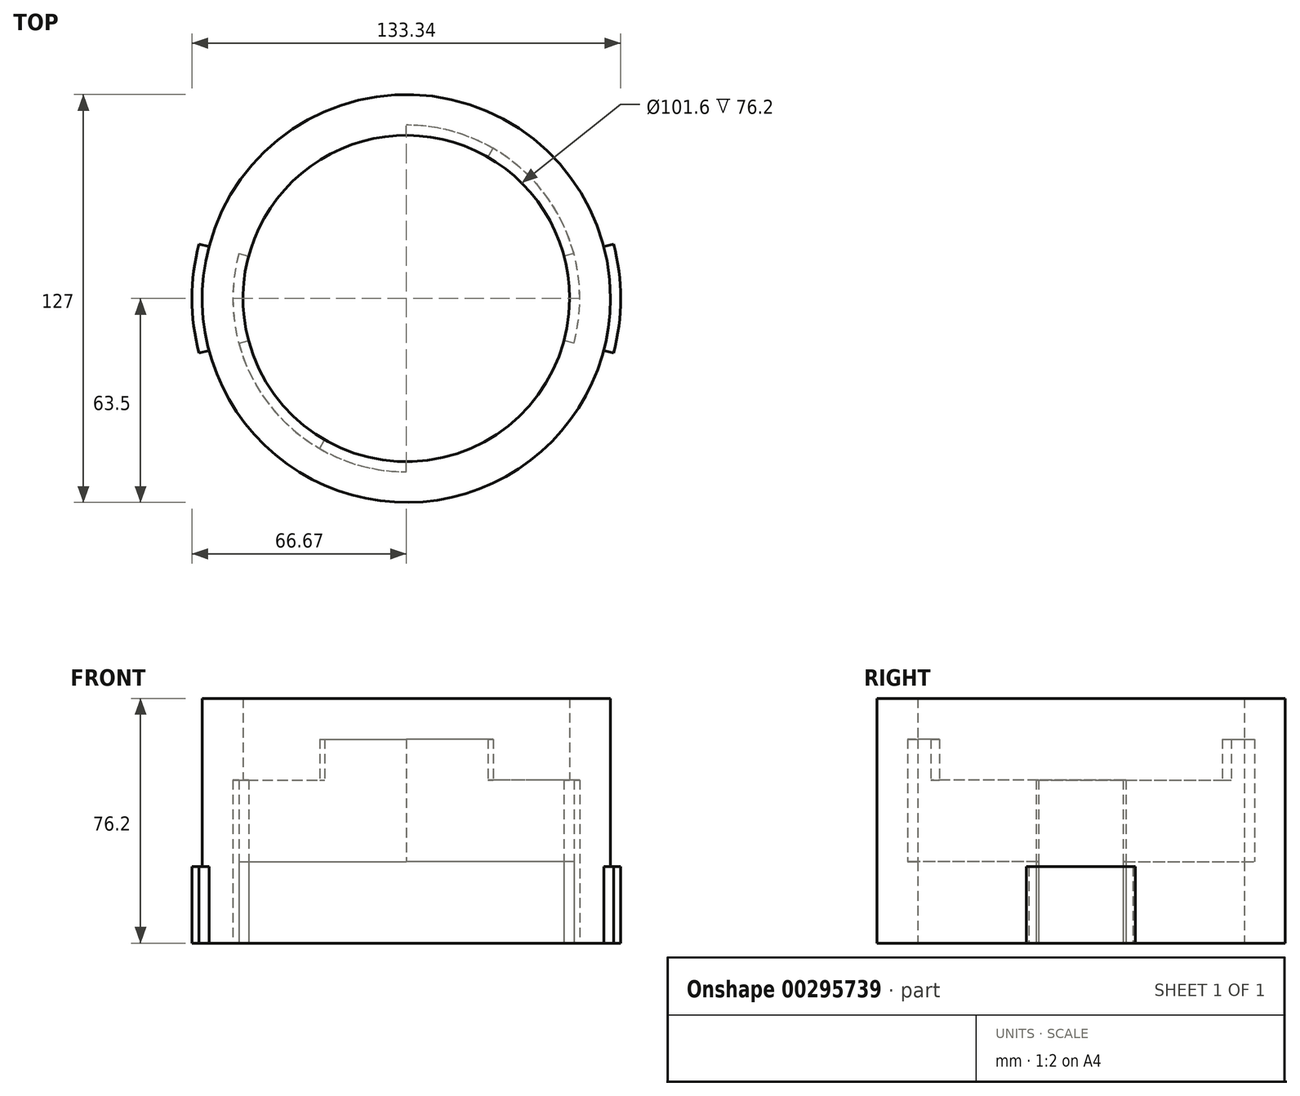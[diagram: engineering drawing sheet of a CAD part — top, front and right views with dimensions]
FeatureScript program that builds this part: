
annotation { "Feature Type Name" : "Feature", "Feature Type Description" : "" }
export const myFeature = defineFeature(function(context is Context, id is Id, definition is map)
    precondition{}
    {
        {
            var Q0;
            Q0=qCreatedBy(makeId("Top.planeOp"),FACE);
            var sketch = newSketch(context, id + "F0", { "sketchPlane" : qUnion([Q0])});
            skCircle(sketch, "E0", {"center": v(0, 0) * mm, "radius": 63.5 * mm});
            skCircle(sketch, "E1", {"center": v(0, 0) * mm, "radius": 50.8 * mm});
            skCircle(sketch, "E2", {"center": v(0, 0) * mm, "radius": 53.98 * mm});
            skArc(sketch, "E3", {"start": v(-64.48, 16.98) * mm, "mid": v(-66.68, 0) * mm, "end": v(-64.48, -16.98) * mm});
            skLineSegment(sketch, "E4.trimOffspring", {"start": v(-61.4, -16.17) * mm, "end": v(-64.48, -16.98) * mm});
            skArc(sketch, "E5.trimOffspring", {"start": v(64.48, -16.98) * mm, "mid": v(66.68, 0) * mm, "end": v(64.48, 16.98) * mm});
            skLineSegment(sketch, "E6.MirrorCS", {"start": v(-61.4, 16.17) * mm, "end": v(-64.48, 16.98) * mm});
            skLineSegment(sketch, "E7.MirrorCS", {"start": v(61.4, -16.17) * mm, "end": v(64.48, -16.98) * mm});
            skLineSegment(sketch, "E8.MirrorCS", {"start": v(61.4, 16.17) * mm, "end": v(64.48, 16.98) * mm});
            skLineSegment(sketch, "E9", {"start": v(0, -53.98) * mm, "end": v(0, -50.8) * mm});
            skLineSegment(sketch, "E10.trimOffspring", {"start": v(0, 50.8) * mm, "end": v(0, 53.98) * mm});
            skLineSegment(sketch, "E11", {"start": v(-26.99, -46.74) * mm, "end": v(-25.4, -44) * mm});
            skLineSegment(sketch, "E12.trimOffspring", {"start": v(25.4, 44) * mm, "end": v(26.99, 46.74) * mm});
            skLineSegment(sketch, "E13", {"start": v(-52.14, -13.97) * mm, "end": v(-49.07, -13.15) * mm});
            skLineSegment(sketch, "E14.MirrorCS", {"start": v(-52.14, 13.97) * mm, "end": v(-49.07, 13.15) * mm});
            skLineSegment(sketch, "E15.MirrorCS", {"start": v(52.14, -13.97) * mm, "end": v(49.07, -13.15) * mm});
            skLineSegment(sketch, "E16.MirrorCS", {"start": v(52.14, 13.97) * mm, "end": v(49.07, 13.15) * mm});
            skSolve(sketch);
        }
        {
            var Q0;
            {var subQ0=sQuery(id+"F0.wireOp",EDGE,"E0");var subQ4=makeQuery(id+"F0.imprint","INTERSECT",VERTEX,{"derivedFrom":[subQ0,sQuery(id+"F0.wireOp",EDGE,"6ba6cb8d-4ce4-45d0-8e24-ed4901a20c0e.trimOffspring")]});Q0=makeQuery(id+"F0.imprint","IMPRINT",FACE,{"disambiguationData":[TD([[makeQuery(id+"F0.imprint","IMPRINT",EDGE,{"disambiguationData":[TD([[subQ4,1.0]])],"derivedFrom":subQ0}),1.0]])]});}
            var Q1;
            {var subQ0=sQuery(id+"F0.wireOp",EDGE,"qwwPtYaD-yE2g-ikrO-oplh-1dd26EcHEVAW");Q1=makeQuery(id+"F0.imprint","IMPRINT",FACE,{"disambiguationData":[TD([[makeQuery(id+"F0.imprint","IMPRINT",EDGE,{"derivedFrom":subQ0}),1.0]])]});}
            var Q2;
            {var subQ0=sQuery(id+"F0.wireOp",EDGE,"qwwPtYaD-yE2g-ikrO-oplh-1dd26EcHEVAW");Q2=makeQuery(id+"F0.imprint","IMPRINT",FACE,{"disambiguationData":[TD([[makeQuery(id+"F0.imprint","IMPRINT",EDGE,{"derivedFrom":subQ0}),-1.0]])]});}
            var Q3;
            {var subQ0=sQuery(id+"F0.wireOp",EDGE,"409aa395-0444-4f70-a1e5-7bc4308f40760.MirrorCS");Q3=makeQuery(id+"F0.imprint","IMPRINT",FACE,{"disambiguationData":[TD([[makeQuery(id+"F0.imprint","IMPRINT",EDGE,{"derivedFrom":subQ0}),-1.0]])]});}
            var Q4;
            {var subQ0=sQuery(id+"F0.wireOp",EDGE,"fd11b51b-482c-4218-80d9-868a347ca85e0.MirrorCS");Q4=makeQuery(id+"F0.imprint","IMPRINT",FACE,{"disambiguationData":[TD([[makeQuery(id+"F0.imprint","IMPRINT",EDGE,{"derivedFrom":subQ0}),1.0]])]});}
            var Q5;
            {var subQ0=sQuery(id+"F0.wireOp",EDGE,"E11");Q5=makeQuery(id+"F0.imprint","IMPRINT",FACE,{"disambiguationData":[TD([[makeQuery(id+"F0.imprint","IMPRINT",EDGE,{"derivedFrom":subQ0}),1.0]])]});}
            var Q6;
            {var subQ0=sQuery(id+"F0.wireOp",EDGE,"E13");Q6=makeQuery(id+"F0.imprint","IMPRINT",FACE,{"disambiguationData":[TD([[makeQuery(id+"F0.imprint","IMPRINT",EDGE,{"derivedFrom":subQ0}),1.0]])]});}
            var Q7;
            {var subQ0=sQuery(id+"F0.wireOp",EDGE,"E10.trimOffspring");Q7=makeQuery(id+"F0.imprint","IMPRINT",FACE,{"disambiguationData":[TD([[makeQuery(id+"F0.imprint","IMPRINT",EDGE,{"derivedFrom":subQ0}),1.0]])]});}
            var Q8;
            {var subQ0=sQuery(id+"F0.wireOp",EDGE,"E9");Q8=makeQuery(id+"F0.imprint","IMPRINT",FACE,{"disambiguationData":[TD([[makeQuery(id+"F0.imprint","IMPRINT",EDGE,{"derivedFrom":subQ0}),1.0]])]});}
            var Q9;
            {var subQ0=sQuery(id+"F0.wireOp",EDGE,"E15.MirrorCS");Q9=makeQuery(id+"F0.imprint","IMPRINT",FACE,{"disambiguationData":[TD([[makeQuery(id+"F0.imprint","IMPRINT",EDGE,{"derivedFrom":subQ0}),-1.0]])]});}
            var Q10;
            {var subQ0=sQuery(id+"F0.wireOp",EDGE,"E9");Q10=makeQuery(id+"F0.imprint","IMPRINT",FACE,{"disambiguationData":[TD([[makeQuery(id+"F0.imprint","IMPRINT",EDGE,{"derivedFrom":subQ0}),-1.0]])]});}
            var Q11;
            {var subQ0=sQuery(id+"F0.wireOp",EDGE,"E12.trimOffspring");Q11=makeQuery(id+"F0.imprint","IMPRINT",FACE,{"disambiguationData":[TD([[makeQuery(id+"F0.imprint","IMPRINT",EDGE,{"derivedFrom":subQ0}),-1.0]])]});}
            var Q12;
            {var subQ0=sQuery(id+"F0.wireOp",EDGE,"E10.trimOffspring");Q12=makeQuery(id+"F0.imprint","IMPRINT",FACE,{"disambiguationData":[TD([[makeQuery(id+"F0.imprint","IMPRINT",EDGE,{"derivedFrom":subQ0}),-1.0]])]});}
            extrude(context, id + "F1", {"entities" : qUnion([Q0, Q1, Q2, Q3, Q4, Q5, Q6, Q7, Q8, Q9, Q10, Q11, Q12]), "depth" : 76.2 * mm});
        }
        {
            var Q0;
            Q0=makeQuery(id+"F0.imprint","IMPRINT",FACE,{"disambiguationData":[TD([[makeQuery(id+"F0.imprint","IMPRINT",EDGE,{"derivedFrom":sQuery(id+"F0.wireOp",EDGE,"E3")}),1.0]])]});
            var Q1;
            Q1=makeQuery(id+"F0.imprint","IMPRINT",FACE,{"disambiguationData":[TD([[makeQuery(id+"F0.imprint","IMPRINT",EDGE,{"derivedFrom":sQuery(id+"F0.wireOp",EDGE,"E5.trimOffspring")}),1.0]])]});
            extrude(context, id + "F2", {"entities" : qUnion([Q0, Q1]), "operationType" : NewBodyOperationType.ADD, "depth" : 23.8 * mm});
        }
        {
            var Q0;
            {var subQ0=sQuery(id+"F0.wireOp",EDGE,"E13");Q0=makeQuery(id+"F0.imprint","IMPRINT",FACE,{"disambiguationData":[TD([[makeQuery(id+"F0.imprint","IMPRINT",EDGE,{"derivedFrom":subQ0}),1.0]])]});}
            var Q1;
            {var subQ0=sQuery(id+"F0.wireOp",EDGE,"E15.MirrorCS");Q1=makeQuery(id+"F0.imprint","IMPRINT",FACE,{"disambiguationData":[TD([[makeQuery(id+"F0.imprint","IMPRINT",EDGE,{"derivedFrom":subQ0}),-1.0]])]});}
            var Q2;
            {var subQ0=sQuery(id+"F0.wireOp",EDGE,"E11");Q2=makeQuery(id+"F0.imprint","IMPRINT",FACE,{"disambiguationData":[TD([[makeQuery(id+"F0.imprint","IMPRINT",EDGE,{"derivedFrom":subQ0}),1.0]])]});}
            var Q3;
            {var subQ0=sQuery(id+"F0.wireOp",EDGE,"E12.trimOffspring");Q3=makeQuery(id+"F0.imprint","IMPRINT",FACE,{"disambiguationData":[TD([[makeQuery(id+"F0.imprint","IMPRINT",EDGE,{"derivedFrom":subQ0}),-1.0]])]});}
            extrude(context, id + "F3", {"entities" : qUnion([Q0, Q1, Q2, Q3]), "operationType" : NewBodyOperationType.REMOVE, "depth" : 50.8 * mm});
        }
        {
            var Q0;
            {var subQ0=sQuery(id+"F0.wireOp",EDGE,"E9");Q0=makeQuery(id+"F0.imprint","IMPRINT",FACE,{"disambiguationData":[TD([[makeQuery(id+"F0.imprint","IMPRINT",EDGE,{"derivedFrom":subQ0}),1.0]])]});}
            var Q1;
            {var subQ0=sQuery(id+"F0.wireOp",EDGE,"E10.trimOffspring");Q1=makeQuery(id+"F0.imprint","IMPRINT",FACE,{"disambiguationData":[TD([[makeQuery(id+"F0.imprint","IMPRINT",EDGE,{"derivedFrom":subQ0}),-1.0]])]});}
            extrude(context, id + "F4", {"entities" : qUnion([Q0, Q1]), "operationType" : NewBodyOperationType.REMOVE, "depth" : 63.5 * mm});
        }
        {
            var Q0;
            {var subQ0=sQuery(id+"F0.wireOp",EDGE,"E11");Q0=makeQuery(id+"F0.imprint","IMPRINT",FACE,{"disambiguationData":[TD([[makeQuery(id+"F0.imprint","IMPRINT",EDGE,{"derivedFrom":subQ0}),1.0]])]});}
            var Q1;
            {var subQ0=sQuery(id+"F0.wireOp",EDGE,"E9");Q1=makeQuery(id+"F0.imprint","IMPRINT",FACE,{"disambiguationData":[TD([[makeQuery(id+"F0.imprint","IMPRINT",EDGE,{"derivedFrom":subQ0}),1.0]])]});}
            var Q2;
            {var subQ0=sQuery(id+"F0.wireOp",EDGE,"E12.trimOffspring");Q2=makeQuery(id+"F0.imprint","IMPRINT",FACE,{"disambiguationData":[TD([[makeQuery(id+"F0.imprint","IMPRINT",EDGE,{"derivedFrom":subQ0}),-1.0]])]});}
            var Q3;
            {var subQ0=sQuery(id+"F0.wireOp",EDGE,"E10.trimOffspring");Q3=makeQuery(id+"F0.imprint","IMPRINT",FACE,{"disambiguationData":[TD([[makeQuery(id+"F0.imprint","IMPRINT",EDGE,{"derivedFrom":subQ0}),-1.0]])]});}
            extrude(context, id + "F5", {"entities" : qUnion([Q0, Q1, Q2, Q3]), "operationType" : NewBodyOperationType.ADD, "depth" : 25.4 * mm});
        }
    });
